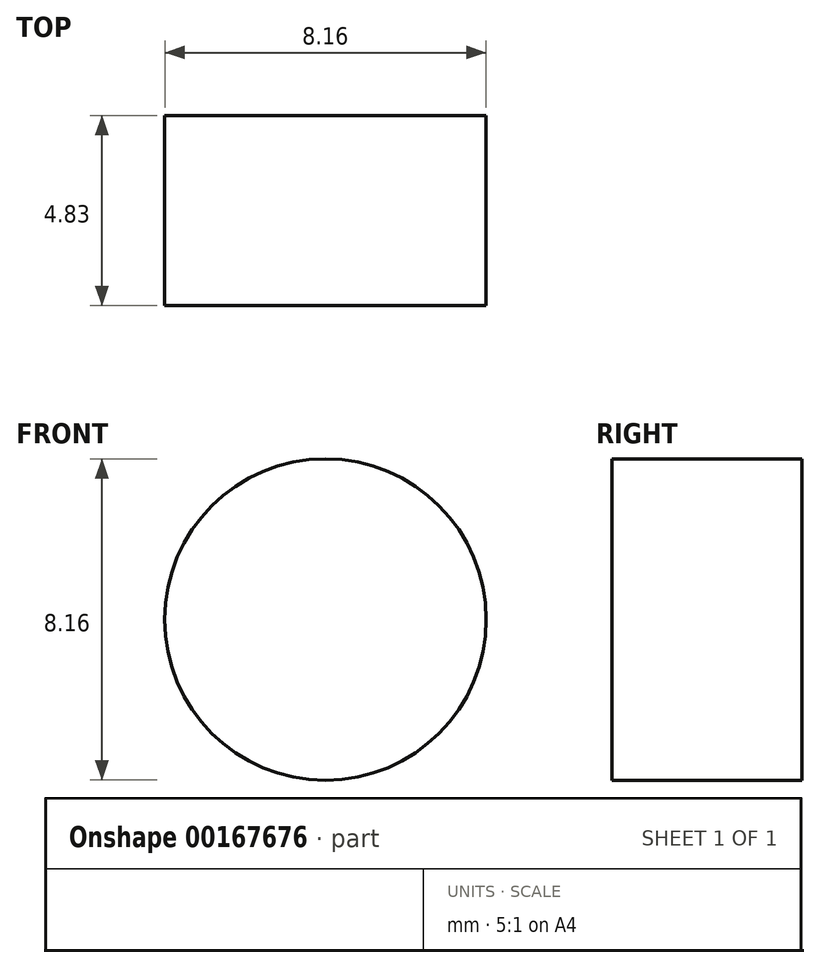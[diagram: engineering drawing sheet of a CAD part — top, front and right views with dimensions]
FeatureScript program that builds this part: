
annotation { "Feature Type Name" : "Feature", "Feature Type Description" : "" }
export const myFeature = defineFeature(function(context is Context, id is Id, definition is map)
    precondition{}
    {
        {
            var Q0;
            Q0=qCreatedBy(makeId("Front.planeOp"),FACE);
            var sketch = newSketch(context, id + "F0", { "sketchPlane" : qUnion([Q0])});
            skCircle(sketch, "E0", {"center": v(0, 0) * mm, "radius": 4.08 * mm});
            skSolve(sketch);
        }
        {
            var Q0;
            Q0=makeQuery(id+"F0.imprint","IMPRINT",FACE,{"disambiguationData":[TD([[makeQuery(id+"F0.imprint","IMPRINT",EDGE,{"derivedFrom":sQuery(id+"F0.wireOp",EDGE,"E0")}),1.0]])]});
            extrude(context, id + "F1", {"entities" : qUnion([Q0]), "depth" : 4.83 * mm});
        }
    });
